FCSTD DOCUMENT  (FreeCAD 1.1R20260325 (Git shallow))
Label: asd
License: All rights reserved
objects: App::DocumentObjectGroup×5, Part::Part2DObjectPython×2
note: 2 computed .brp shape members not serialized (recipe doc carries the construction recipe); baked Part::Feature solids carry a one-line shape summary decoded from their .brp

FEATURE [App::DocumentObjectGroup] Simbolo_2D
FEATURE [App::DocumentObjectGroup] Foto
FEATURE [App::DocumentObjectGroup] Modelo_3D
FEATURE [App::DocumentObjectGroup] Descricao
FEATURE [App::DocumentObjectGroup] Detalhes_2D
FEATURE [Part::Part2DObjectPython] Line  # Draft 2D object (typed FeaturePython)
  Area = 0
  ChamferSize = 0
  Closed = false
  End = (1.21571,0.0109195,0)
  FilletRadius = 0
  Length = 1.23061
  MakeFace = true
  Placement = pos=(-0.0145595,-0.0181992,0) rot=(0,0,1;0rad)
  Points = (2) [(0,0,0),(1.23027,0.0291186,0)]
  Start = (-0.0145595,-0.0181992,0)
  Subdivisions = 0
FEATURE [Part::Part2DObjectPython] Wire  # Draft 2D object (typed FeaturePython)
  Area = 0.64223
  ChamferSize = 0
  Closed = true
  End = (2.58429,-0.0254789,0)
  FilletRadius = 0
  Length = 3.85022
  MakeFace = true
  Placement = pos=(1.17203,-0.389463,0) rot=(0,0,1;0rad)
  Points = (3) [(0,0,0),(0.0582376,0.924519,0),(1.41226,0.363984,0)]
  Start = (1.17203,-0.389463,0)
  Subdivisions = 0
